# Revit family: LEGRAND_PRISES_NON_VERROUILLEES_ENCASTREES_IP66_400
name_source: partatom
category: Installations électriques
revit_build: Autodesk Revit 2018 (Build: 20170223_1515(x64)
units: mm (PartAtom-declared; Revit-internal decimal feet)

## family parameters
Conserver l'orientation des annotations = Non
Cote de connecteur circulaire = Utiliser le diamètre
Couper avec des vides une fois chargée = Non
Hôte = Face
Partagée = Non
Point de calcul de pièce = Non
Type d'élément = Normal

## types (10) — shared parameters
Conditions Générale d'Utilisation = https://export.legrand.com
Couleur caractéristique = rouge
Description = Prise au standard international pour montage encastré ou saillie avec accessoire permet la connexion d'appareils de puissance
Elévation par défaut = 1000 mm
Fabricant = Legrand
Standard CEI ou NFC = CEI
Température maximale d'installation = 40°C
Température maximum d'utilisation = 100°C
Température minimum d'installation = -20°C
Température minimum d'utilisation = -50°C
Tension V = 400 V  50/60 Hz  rouge
Type de cerrouillage = bornes à vis
classe de protection IP = IP66/67-55
installation Encastrée E ou Saillie S = encastré et saillie
matériau du boitier = plastique
résistance aux chocs IK = 09
sans halogène = Non

## per-type parameters (varying)
| type | Dia bouchon | Intensité A | Modèle | Nombre de pôles | Position de la Terre h | RAY BOUCHON | Ray | dIA | entraxe de fixation horizontal mm | entraxe de fixation vertical mm | h1 | hauteur mm | largeur mm | profondeur d'encastrement mm | profondeur mm |
| Socle tableau Hypra   IP66/67-55   16 A   380/415 V   3P+T   plast | 79 mm | 16 A | 051130 | 4 | 6 | 40 mm | 26 mm | 53 mm | 60 mm | 70 mm | 50 mm  [stored 0.164042 ft] | 84 mm | 74 mm | 41 mm | 89 mm  [stored 0.291995 ft] |
| Socle tableau Hypra   IP66/67-55   16 A   380/415 V   3P+N+T   plast | 82 mm | 16 A | 051131 | 6 | 6 | 41 mm | 27 mm | 55 mm | 60 mm | 70 mm | 50 mm  [stored 0.164042 ft] | 84 mm | 80 mm | 42 mm  [stored 0.137795 ft] | 92 mm |
| Socle tableau entraxe unifié Hypra  IP66/67-55  16 A   380/415 V   3P+T   plast | 84 mm | 16 A | 051150 | 4 | 6 | 42 mm  [stored 0.137795 ft] | 28 mm | 56 mm | 70 mm | 70 mm | 50 mm  [stored 0.164042 ft] | 84 mm | 84 mm | 43 mm | 84 mm |
| Socle tableau entraxe unifié Hypra  IP66/67-55  16 A  380/415 V   3P+N+T  plast | 84 mm | 16 A | 051151 | 5 | 6 | 42 mm  [stored 0.137795 ft] | 28 mm | 56 mm | 70 mm | 70 mm | 50 mm  [stored 0.164042 ft] | 84 mm | 84 mm | 43 mm | 84 mm |
| Socle tableau entraxe unifié Hypra  IP66/67-55  32 A   380/415 V   3P+T   plast | 89 mm  [stored 0.291995 ft] | 32 A | 053050 | 4 | 6 | 45 mm | 30 mm  [stored 0.0984252 ft] | 59 mm | 70 mm | 70 mm | 56 mm | 94 mm | 84 mm | 54 mm | 104 mm |
| Socle tableau entraxe unifié Hypra  IP66/67-55  32 A  380/415 V   3P+N+T  plast | 89 mm  [stored 0.291995 ft] | 32 A | 053051 | 5 | 6 | 45 mm | 30 mm  [stored 0.0984252 ft] | 59 mm | 70 mm | 70 mm | 56 mm | 94 mm | 84 mm | 54 mm | 105 mm  [stored 0.344488 ft] |
| Socle de tableau Hypra  IP66/67-55   63A   380 415 V   3P+T   plast | 106 mm | 63 A | 059427 | 4 | 9 | 53 mm | 35 mm | 71 mm | 77 mm | 85 mm | 64 mm | 106 mm | 106 mm | 85 mm | 164 mm |
| Socle de tableau Hypra  IP66/67-55   63A   380 415 V   3P+N+T   plast | 106 mm | 63 A | 059428 | 4 | 9 | 53 mm | 35 mm | 71 mm | 77 mm | 85 mm | 64 mm | 106 mm | 106 mm | 85 mm | 164 mm |
| Socle de tableau Hypra  IP66/67-55   125A   380 415 V   3P+T   plast | 146 mm  [stored 0.479003 ft] | 125 A | 059512 | 4 | 6 | 73 mm  [stored 0.239501 ft] | 49 mm | 97 mm | 124 mm | 124 mm | 88 mm | 146 mm  [stored 0.479003 ft] | 146 mm  [stored 0.479003 ft] | 84 mm | 180 mm |
| Socle de tableau Hypra  IP66/67-55   125A   380 415 V   3P+N+T   plast | 146 mm  [stored 0.479003 ft] | 125 A | 059513 | 5 | 6 | 73 mm  [stored 0.239501 ft] | 49 mm | 97 mm | 124 mm | 124 mm | 88 mm | 146 mm  [stored 0.479003 ft] | 146 mm  [stored 0.479003 ft] | 84 mm | 180 mm |

note: [stored X ft] marks values corroborated as IEEE doubles in the binary element streams (Revit-internal decimal feet)
